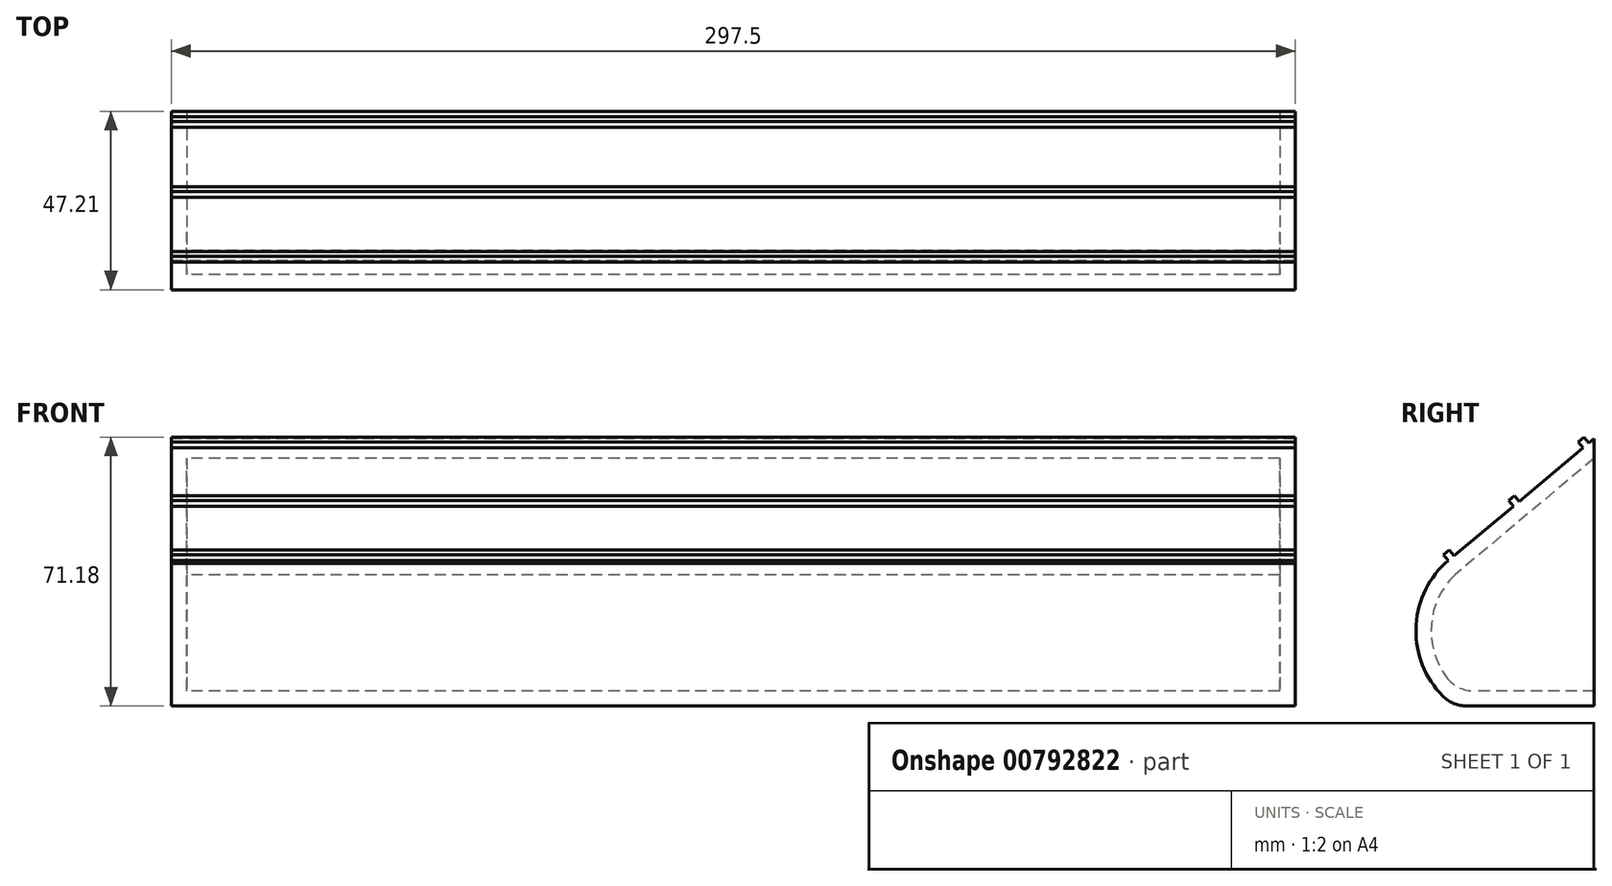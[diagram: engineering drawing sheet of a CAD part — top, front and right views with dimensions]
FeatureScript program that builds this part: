
annotation { "Feature Type Name" : "Feature", "Feature Type Description" : "" }
export const myFeature = defineFeature(function(context is Context, id is Id, definition is map)
    precondition{}
    {
        {
            var Q0;
            Q0=qCreatedBy(makeId("Right.planeOp"),FACE);
            var sketch = newSketch(context, id + "F0", { "sketchPlane" : qUnion([Q0])});
            skLineSegment(sketch, "E0", {"start": v(-535.73, -8.28) * mm, "end": v(-572.73, -8.28) * mm});
            skArc(sketch, "E1", {"start": v(-575.3, 29.42) * mm, "mid": v(-582.89, 9.96) * mm, "end": v(-572.73, -8.28) * mm});
            skLineSegment(sketch, "E2", {"start": v(-535.73, -8.28) * mm, "end": v(-535.73, 62.53) * mm});
            skLineSegment(sketch, "E3", {"start": v(-535.73, 62.53) * mm, "end": v(-575.3, 29.42) * mm});
            skLineSegment(sketch, "E4", {"start": v(-574.33, 30.22) * mm, "end": v(-575.62, 31.76) * mm});
            skLineSegment(sketch, "E5", {"start": v(-575.62, 31.76) * mm, "end": v(-574.08, 33.04) * mm});
            skLineSegment(sketch, "E6", {"start": v(-537.12, 61.36) * mm, "end": v(-538.4, 62.9) * mm});
            skLineSegment(sketch, "E7", {"start": v(-538.4, 62.9) * mm, "end": v(-539.94, 61.61) * mm});
            skLineSegment(sketch, "E8", {"start": v(-539.94, 61.61) * mm, "end": v(-538.4, 59.78) * mm});
            skLineSegment(sketch, "E9", {"start": v(-555.62, 45.88) * mm, "end": v(-556.9, 47.42) * mm});
            skLineSegment(sketch, "E10", {"start": v(-556.9, 47.42) * mm, "end": v(-558.44, 46.13) * mm});
            skLineSegment(sketch, "E11", {"start": v(-558.44, 46.13) * mm, "end": v(-556.9, 44.3) * mm});
            skLineSegment(sketch, "E12", {"start": v(-574.08, 33.04) * mm, "end": v(-572.8, 31.5) * mm});
            skSolve(sketch);
        }
        {
            var Q0;
            Q0=qSketchRegion(id+"F0",true);
            extrude(context, id + "F1", {"entities" : qUnion([Q0]), "depth" : 55.5 * mm, "offsetDistance" : 25 * mm});
        }
        {
            var Q0;
            Q0 = qSketchRegion(id + "F0", true);
            extrude(context, id + "F2", {"entities" : qUnion([Q0]), "operationType" : NewBodyOperationType.ADD, "depth" : 297.5 * mm, "offsetDistance" : 25 * mm});
        }
        {
            var Q0;
            {var subQ0=sQuery(id+"F0.wireOp",EDGE,"UzuzuQkW-eQ3q-EAej-YN0D-F1dVNnh89gvl");var subQ1=sQuery(id+"F0.wireOp",EDGE,"6QLN2nIx-mnyv-eBxz-DGQy-tApPfC4bbUGP");Q0=makeQuery(id+"F2.boolean.opBoolean","MERGE",FACE,{"derivedFrom":[makeQuery(id+"F1.opExtrude","SWEPT_FACE",FACE,{"disambiguationData":[OSD([subQ1,subQ0])]}),makeQuery(id+"F2.opExtrude","SWEPT_FACE",FACE,{"disambiguationData":[OSD([subQ1,subQ0])]})]});}
            var Q1;
            {var subQ0=sQuery(id+"F0.wireOp",EDGE,"E2");Q1=makeQuery(id+"F2.boolean.opBoolean","MERGE",FACE,{"derivedFrom":[makeQuery(id+"F1.opExtrude","SWEPT_FACE",FACE,{"disambiguationData":[OSD([subQ0])]}),makeQuery(id+"F2.opExtrude","SWEPT_FACE",FACE,{"disambiguationData":[OSD([subQ0])]})]});}
            shell(context, id + "F3", {"entities" : qUnion([Q0, Q1]), "thickness" : 4 * mm});
        }
        {
            var Q0;
            {var subQ0=sQuery(id+"F0.wireOp",EDGE,"E1");var subQ1=sQuery(id+"F0.wireOp",EDGE,"E0");Q0=makeQuery(id+"F2.boolean.opBoolean","MERGE",EDGE,{"derivedFrom":[makeQuery(id+"F1.opExtrude","SWEPT_EDGE",EDGE,{"disambiguationData":[OSD([subQ1,subQ0])]}),makeQuery(id+"F2.opExtrude","SWEPT_EDGE",EDGE,{"disambiguationData":[OSD([subQ1,subQ0])]})]});}
            fillet(context, id + "F4", {"entities" : qUnion([Q0]), "radius" : 9 * mm, "tangentPropagation" : true, "allowEdgeOverflow" : false});
        }
        {
            var Q0;
            Q0=makeQuery(id+"F3.opShell","OFFSET_EDGE",EDGE,{"disambiguationData":[OSD([sQuery(id+"F0.wireOp",EDGE,"E0"),sQuery(id+"F0.wireOp",EDGE,"E1")])]});
            fillet(context, id + "F5", {"entities" : qUnion([Q0]), "radius" : 9 * mm, "tangentPropagation" : true, "allowEdgeOverflow" : false});
        }
    });
